SOLIDWORKS PART (.sldprt)
format: sldprt  version: not decoded by parser v0  size: 139,264 bytes
history: native  units: mm
features: sketch x8, extrude x5, plane x3, fillet x1, revolve x1 (+7 scaffold rows collapsed)
feature tree (25):
  scaffold x7  (default folders/planes/origin — collapsed)
  plane  "front x-y"
  plane  "top y-z"
  plane  "side x-z"
  sketch  "Sketch1"  dims[D1=203.2mm]
  extrude  "Base-Extrude"  Depth=254mm
  fillet  "Fillet2"  Radius=50.8mm
  sketch  "Sketch3"  dims[D1=25.4mm]
  extrude  "Boss-Extrude2"  Depth=25.4mm
  sketch  "Sketch4"
  sketch  "Sketch5"  dims[D1=25.4mm]
  revolve  "Boss-Revolve1"  Angle=180deg
  sketch  "Sketch6"
  sketch  "Sketch7"
  extrude  "Split Line2"  [1 undecoded]
  sketch  "Sketch8"
  extrude  "Split Line3"  [1 undecoded]
  sketch  "Sketch9"
  extrude  "Split Line4"  [1 undecoded]
decode coverage: 7 of 15 modeling features carry decoded parameters
note: 3 parameter values undecoded
summary: no parameter record found for 3 features
note: suppression state not decoded; provenance and decode notes live in map.json
